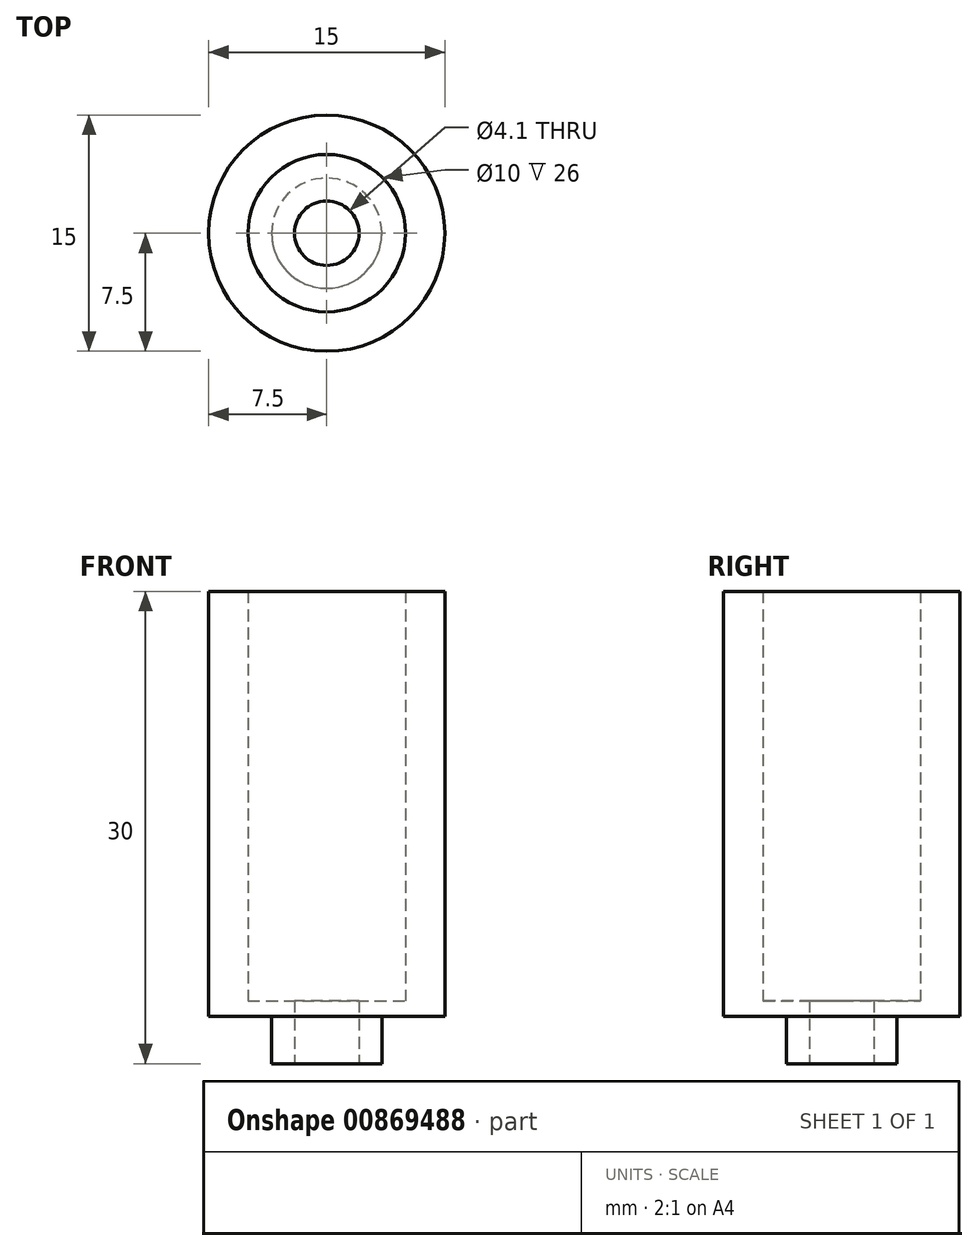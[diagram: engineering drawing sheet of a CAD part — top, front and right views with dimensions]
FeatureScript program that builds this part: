
annotation { "Feature Type Name" : "Feature", "Feature Type Description" : "" }
export const myFeature = defineFeature(function(context is Context, id is Id, definition is map)
    precondition{}
    {
        {
            var Q0;
            Q0=qCreatedBy(makeId("Top.planeOp"),FACE);
            var sketch = newSketch(context, id + "F0", { "sketchPlane" : qUnion([Q0])});
            skCircle(sketch, "E0", {"center": v(0, 0) * mm, "radius": 7.5 * mm});
            skSolve(sketch);
        }
        {
            var Q0;
            Q0 = qSketchRegion(id + "F0", true);
            extrude(context, id + "F1", {"entities" : qUnion([Q0]), "depth" : 30 * mm, "offsetDistance" : 25 * mm});
        }
        {
            var Q0;
            Q0=qCreatedBy(makeId("Top.planeOp"),FACE);
            var sketch = newSketch(context, id + "F2", { "sketchPlane" : qUnion([Q0])});
            skCircle(sketch, "E1", {"center": v(0, 0) * mm, "radius": 2.05 * mm});
            skSolve(sketch);
        }
        {
            var Q0;
            Q0 = qSketchRegion(id + "F2", true);
            extrude(context, id + "F3", {"entities" : qUnion([Q0]), "operationType" : NewBodyOperationType.REMOVE, "depth" : 4 * mm, "offsetDistance" : 25 * mm});
        }
        {
            var Q0;
            Q0=makeQuery(id+"F3.boolean.opBoolean","COPY",FACE,{"derivedFrom":makeQuery(id+"F3.opExtrude","CAP_FACE",FACE,{"disambiguationData":[OSD([sQuery(id+"F2.wireOp",EDGE,"E1")])],"isStart":false})});
            cPlane(context, id + "F4", {"entities" : qUnion([Q0]), "cplaneType" : CPlaneType.OFFSET, "offset" : 0 * mm, "width" : 150 * mm, "height" : 150 * mm});
        }
        {
            var Q0;
            Q0=qCreatedBy(id+"F4.planeOp",FACE);
            var sketch = newSketch(context, id + "F5", { "sketchPlane" : qUnion([Q0])});
            skCircle(sketch, "E2", {"center": v(0, 0) * mm, "radius": 5 * mm});
            skSolve(sketch);
        }
        {
            var Q0;
            Q0 = qSketchRegion(id + "F5", true);
            var Q1;
            Q1=makeQuery(id+"F1.opExtrude","CAP_FACE",FACE,{"disambiguationData":[OSD([sQuery(id+"F0.wireOp",EDGE,"E0")])],"isStart":false});
            extrude(context, id + "F6", {"entities" : qUnion([Q0]), "operationType" : NewBodyOperationType.REMOVE, "endBound" : BoundingType.UP_TO_SURFACE, "oppositeDirection" : true, "depth" : 25 * mm, "endBoundEntityFace" : qUnion([Q1]), "offsetDistance" : 25 * mm});
        }
        {
            var Q0;
            Q0=makeQuery(id+"F1.opExtrude","CAP_FACE",FACE,{"disambiguationData":[OSD([sQuery(id+"F0.wireOp",EDGE,"E0")])],"isStart":true});
            cPlane(context, id + "F7", {"entities" : qUnion([Q0]), "cplaneType" : CPlaneType.OFFSET, "offset" : 3 * mm, "oppositeDirection" : true, "width" : 150 * mm, "height" : 150 * mm});
        }
        {
            var Q0;
            Q0=qCreatedBy(id+"F7.planeOp",FACE);
            var sketch = newSketch(context, id + "F8", { "sketchPlane" : qUnion([Q0])});
            skCircle(sketch, "E3", {"center": v(0, 0) * mm, "radius": 3.5 * mm});
            skCircle(sketch, "E4", {"center": v(0, 0) * mm, "radius": 7.5 * mm});
            skSolve(sketch);
        }
        {
            var Q0;
            Q0 = qSketchRegion(id + "F8", true);
            var Q1;
            Q1=makeQuery(id+"F1.opExtrude","CAP_FACE",FACE,{"disambiguationData":[OSD([sQuery(id+"F0.wireOp",EDGE,"E0")])],"isStart":true});
            extrude(context, id + "F9", {"entities" : qUnion([Q0]), "operationType" : NewBodyOperationType.REMOVE, "endBound" : BoundingType.UP_TO_SURFACE, "depth" : 25 * mm, "endBoundEntityFace" : qUnion([Q1]), "offsetDistance" : 25 * mm});
        }
    });
